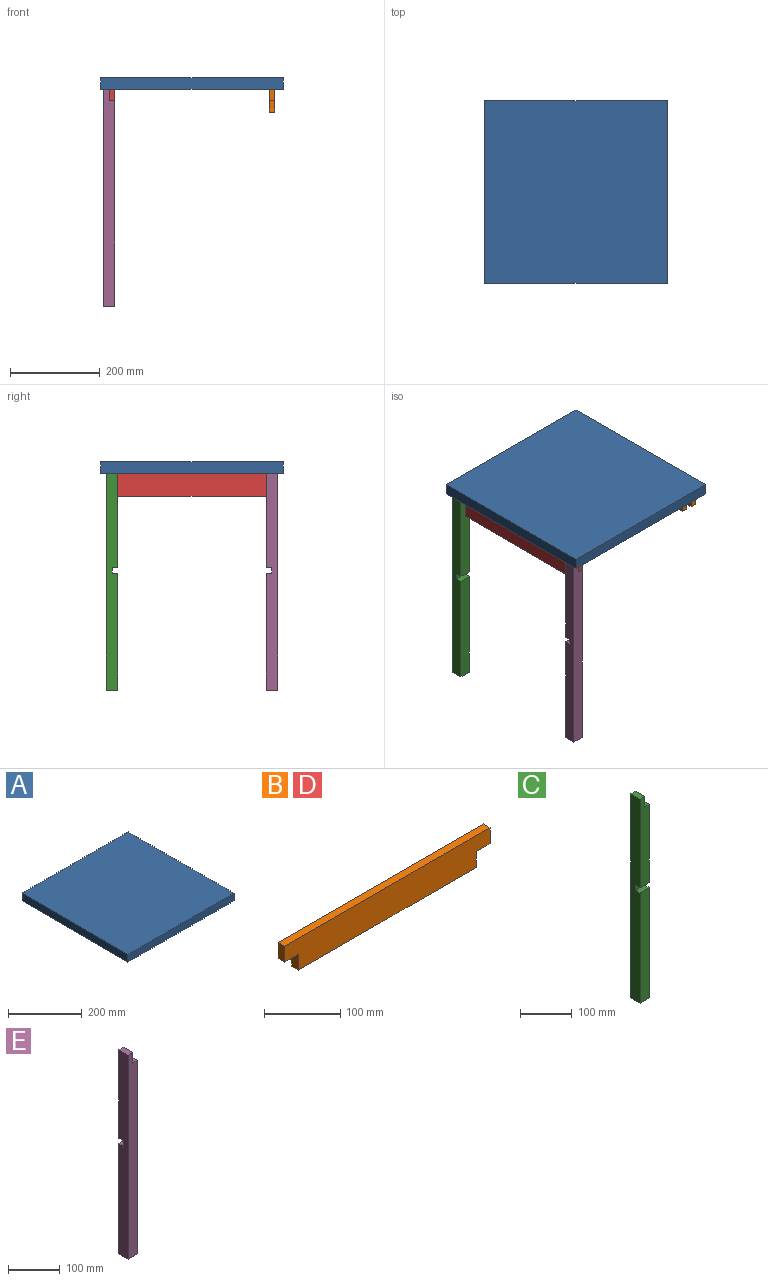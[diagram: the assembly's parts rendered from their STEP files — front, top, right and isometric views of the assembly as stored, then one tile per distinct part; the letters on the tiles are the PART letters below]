
ASSEMBLY  parts=5 mates=4
PART A: 6 faces, bbox 406.4x406.4x25.4 mm
  f0: plane 406.4x406.4mm, normal (0,0,1), area 165161mm2, adj f1,f3,f4,f5
  f1: plane 406.4x25.4mm, normal (-1,0,0), area 10322.6mm2, adj f0,f2,f4,f5
  f2: plane 406.4x406.4mm, normal (0,0,-1), area 165161mm2, adj f1,f3,f4,f5
  f3: plane 406.4x25.4mm, normal (1,0,0), area 10322.6mm2, adj f0,f2,f4,f5
  f4: plane 406.4x25.4mm, normal (0,-1,0), area 10322.6mm2, adj f0,f1,f2,f3
  f5: plane 406.4x25.4mm, normal (0,1,0), area 10322.6mm2, adj f0,f1,f2,f3
PART B: 10 faces, bbox 381x12.7x50.8 mm
  f0: plane 25.4x12.7mm, normal (0,0,-1), area 322.6mm2, adj f1,f7,f8,f9
  f1: plane 25.4x12.7mm, normal (-1,0,0), area 322.6mm2, adj f0,f2,f8,f9
  f2: plane 330.2x12.7mm, normal (0,0,-1), area 4193.5mm2, adj f1,f3,f8,f9
  f3: plane 25.4x12.7mm, normal (1,0,0), area 322.6mm2, adj f2,f4,f8,f9
  f4: plane 25.4x12.7mm, normal (0,0,-1), area 322.6mm2, adj f3,f5,f8,f9
  f5: plane 25.4x12.7mm, normal (1,0,0), area 322.6mm2, adj f4,f6,f8,f9
  f6: plane 381x12.7mm, normal (0,0,1), area 4838.7mm2, adj f5,f7,f8,f9
  f7: plane 25.4x12.7mm, normal (-1,0,0), area 322.6mm2, adj f0,f6,f8,f9
  f8: plane 381x50.8mm, normal (0,-1,0), area 18064.5mm2, adj f0,f1,f2,f3,f4,f5,f6,f7
  f9: plane 381x50.8mm, normal (0,1,0), area 18064.5mm2, adj f0,f1,f2,f3,f4,f5,f6,f7
PART C: 12 faces, bbox 25.4x25.4x482.6 mm
  f0: plane 260.35x25.4mm, normal (0,-1,0), area 6612.9mm2, adj f1,f2,f3,f9
  f1: plane 457.2x25.4mm, normal (1,0,0), area 11451.6mm2, adj f0,f3,f4,f7,f8,f9,f10,f11
  f2: plane 482.6x25.4mm, normal (-1,0,0), area 12096.8mm2, adj f0,f3,f6,f7,f8,f9,f10,f11
  f3: plane 25.4x25.4mm, normal (0,0,-1), area 645.2mm2, adj f0,f1,f2,f8
  f4: plane 25.4x12.7mm, normal (0,0,1), area 322.6mm2, adj f1,f5,f7,f8
  f5: plane 25.4x25.4mm, normal (1,0,0), area 645.2mm2, adj f4,f6,f7,f8
  f6: plane 25.4x12.7mm, normal (0,0,1), area 322.6mm2, adj f2,f5,f7,f8
  f7: plane 209.55x25.4mm, normal (0,-1,0), area 5000mm2, adj f1,f2,f4,f5,f6,f10
  f8: plane 482.6x25.4mm, normal (0,1,0), area 11935.5mm2, adj f1,f2,f3,f4,f5,f6
  f9: plane 25.4x12.7mm, normal (0,0,1), area 322.6mm2, adj f0,f1,f2,f11
  f10: plane 25.4x12.7mm, normal (0,0,-1), area 322.6mm2, adj f1,f2,f7,f11
  f11: plane 25.4x12.7mm, normal (0,-1,0), area 322.6mm2, adj f1,f2,f9,f10
PART D: same geometry as B
PART E: 12 faces, bbox 25.4x25.4x482.6 mm
  f0: plane 260.35x25.4mm, normal (0,1,0), area 6612.9mm2, adj f2,f3,f4,f9
  f1: plane 209.55x25.4mm, normal (0,1,0), area 5000mm2, adj f2,f3,f5,f6,f7,f10
  f2: plane 457.2x25.4mm, normal (1,0,0), area 11451.6mm2, adj f0,f1,f4,f5,f8,f9,f10,f11
  f3: plane 482.6x25.4mm, normal (-1,0,0), area 12096.8mm2, adj f0,f1,f4,f7,f8,f9,f10,f11
  f4: plane 25.4x25.4mm, normal (0,0,-1), area 645.2mm2, adj f0,f2,f3,f8
  f5: plane 25.4x12.7mm, normal (0,0,1), area 322.6mm2, adj f1,f2,f6,f8
  f6: plane 25.4x25.4mm, normal (1,0,0), area 645.2mm2, adj f1,f5,f7,f8
  f7: plane 25.4x12.7mm, normal (0,0,1), area 322.6mm2, adj f1,f3,f6,f8
  f8: plane 482.6x25.4mm, normal (0,-1,0), area 11935.5mm2, adj f2,f3,f4,f5,f6,f7
  f9: plane 25.4x12.7mm, normal (0,0,1), area 322.6mm2, adj f0,f2,f3,f11
  f10: plane 25.4x12.7mm, normal (0,0,-1), area 322.6mm2, adj f1,f2,f3,f11
  f11: plane 25.4x12.7mm, normal (0,1,0), area 322.6mm2, adj f2,f3,f9,f10
PLACE A rot(axis=(0,0,1),90deg) t=(-760.34,374.29,-138.28)mm
PLACE B rot(axis=(0,0,1),90deg) t=(-385.69,354.2,-198.39)mm
PLACE C t=(-695.78,617.51,-350.28)mm
PLACE D rot(axis=(0,0,1),90deg) t=(-741.29,354.2,-198.39)mm
PLACE E t=(-695.78,261.91,-350.28)mm
MATE fastened A.f2 <-> D.f6  axis (0,0,-1) through (-760.34,427.01,-155.78)mm
MATE fastened B.f6 <-> A.f2  axis (0,0,1) through (-379.34,427.01,-155.78)mm
MATE fastened D.f4 <-> C.f4  axis (0,0,-1) through (-734.94,604.81,-181.18)mm
MATE fastened E.f5 <-> D.f0  axis (0,0,1) through (-734.94,249.21,-181.18)mm
